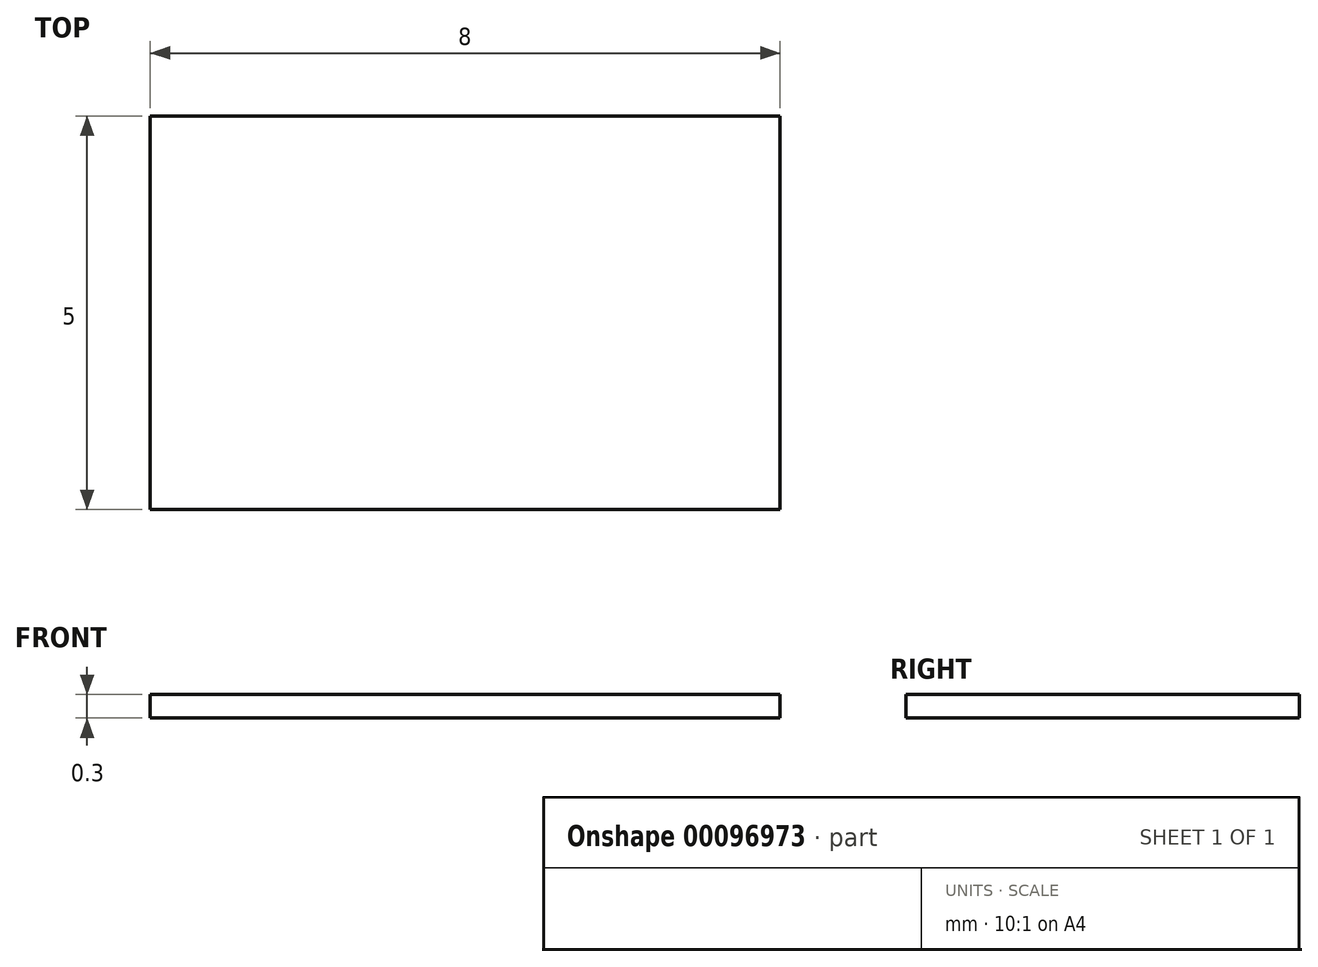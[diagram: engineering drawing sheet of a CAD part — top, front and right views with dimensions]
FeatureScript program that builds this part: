
annotation { "Feature Type Name" : "Feature", "Feature Type Description" : "" }
export const myFeature = defineFeature(function(context is Context, id is Id, definition is map)
    precondition{}
    {
        {
            var Q0;
            Q0=qCreatedBy(makeId("Top.planeOp"),FACE);
            var sketch = newSketch(context, id + "F0", { "sketchPlane" : qUnion([Q0])});
            skLineSegment(sketch, "E0.bottom", {"start": v(4, 2.5) * mm, "end": v(-4, 2.5) * mm});
            skLineSegment(sketch, "E0.top", {"start": v(4, -2.5) * mm, "end": v(-4, -2.5) * mm});
            skLineSegment(sketch, "E0.left", {"start": v(4, 2.5) * mm, "end": v(4, -2.5) * mm});
            skLineSegment(sketch, "E0.right", {"start": v(-4, 2.5) * mm, "end": v(-4, -2.5) * mm});
            skPoint(sketch, "E0.middle", {"position": v(0, 0) * mm});
            skSolve(sketch);
        }
        {
            var Q0;
            Q0 = qSketchRegion(id + "F0", true);
            extrude(context, id + "F1", {"entities" : qUnion([Q0]), "depth" : .3 * mm});
        }
    });
